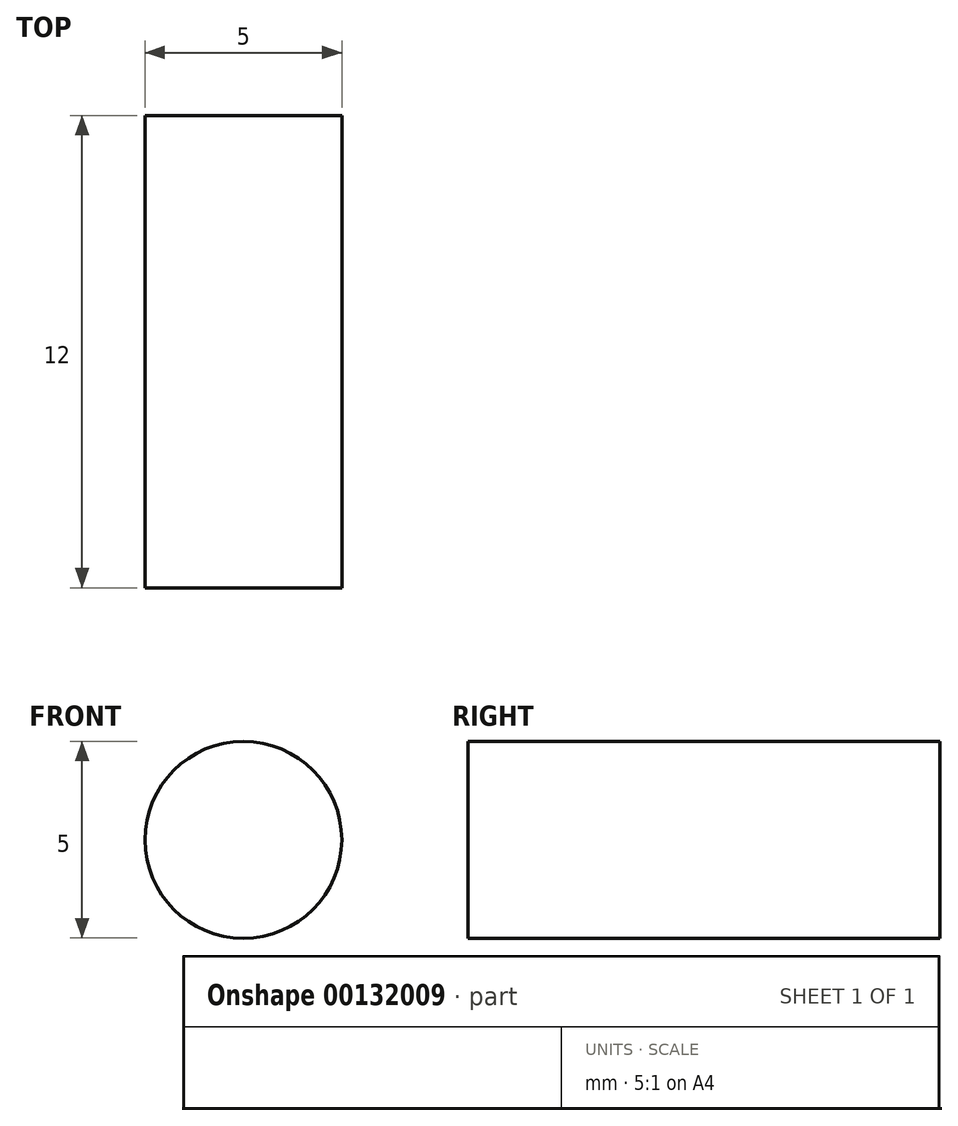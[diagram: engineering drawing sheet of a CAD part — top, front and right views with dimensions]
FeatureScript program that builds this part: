
annotation { "Feature Type Name" : "Feature", "Feature Type Description" : "" }
export const myFeature = defineFeature(function(context is Context, id is Id, definition is map)
    precondition{}
    {
        {
            var Q0;
            Q0=qCreatedBy(makeId("Front.planeOp"),FACE);
            var sketch = newSketch(context, id + "F0", { "sketchPlane" : qUnion([Q0])});
            skCircle(sketch, "E0", {"center": v(-23.81, 16.45) * mm, "radius": 2.5 * mm});
            skSolve(sketch);
        }
        {
            var Q0;
            Q0=makeQuery(id+"F0.imprint","IMPRINT",FACE,{"disambiguationData":[TD([[makeQuery(id+"F0.imprint","IMPRINT",EDGE,{"derivedFrom":sQuery(id+"F0.wireOp",EDGE,"E0")}),1.0]])]});
            extrude(context, id + "F1", {"entities" : qUnion([Q0]), "depth" : 12 * mm});
        }
    });
